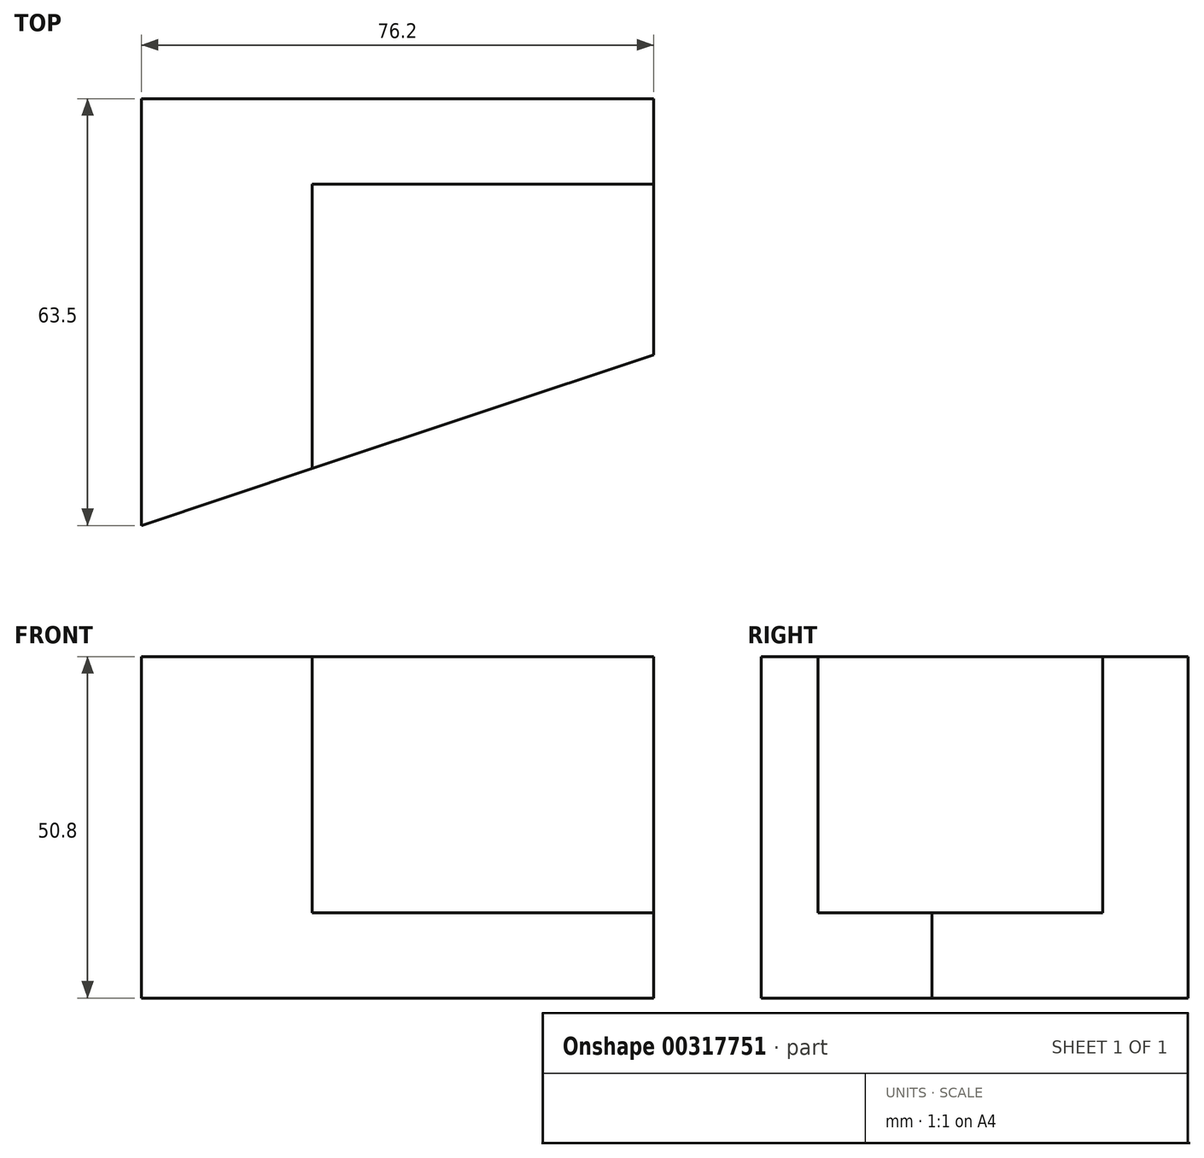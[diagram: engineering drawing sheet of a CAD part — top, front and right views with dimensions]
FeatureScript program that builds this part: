
annotation { "Feature Type Name" : "Feature", "Feature Type Description" : "" }
export const myFeature = defineFeature(function(context is Context, id is Id, definition is map)
    precondition{}
    {
        {
            var Q0;
            Q0=qCreatedBy(makeId("Top.planeOp"),FACE);
            var sketch = newSketch(context, id + "F0", { "sketchPlane" : qUnion([Q0])});
            skLineSegment(sketch, "E0.bottom", {"start": v(0, 0) * mm, "end": v(76.2, 0) * mm});
            skLineSegment(sketch, "E0.top", {"start": v(0, 63.5) * mm, "end": v(76.2, 63.5) * mm});
            skLineSegment(sketch, "E0.left", {"start": v(0, 0) * mm, "end": v(0, 63.5) * mm});
            skLineSegment(sketch, "E0.right", {"start": v(76.2, 0) * mm, "end": v(76.2, 63.5) * mm});
            skSolve(sketch);
        }
        {
            var Q0;
            Q0 = qSketchRegion(id + "F0", true);
            extrude(context, id + "F1", {"entities" : qUnion([Q0]), "depth" : 12.7 * mm});
        }
        {
            var Q0;
            Q0=makeQuery(id+"F1.opExtrude","CAP_FACE",FACE,{"disambiguationData":[OSD([sQuery(id+"F0.wireOp",EDGE,"E0.bottom"),sQuery(id+"F0.wireOp",EDGE,"E0.top"),sQuery(id+"F0.wireOp",EDGE,"E0.left"),sQuery(id+"F0.wireOp",EDGE,"E0.right")])],"isStart":false});
            var sketch = newSketch(context, id + "F2", { "sketchPlane" : qUnion([Q0])});
            skLineSegment(sketch, "E1.bottom", {"start": v(0, 0) * mm, "end": v(25.4, 0) * mm});
            skLineSegment(sketch, "E1.top", {"start": v(0, 63.5) * mm, "end": v(25.4, 63.5) * mm});
            skLineSegment(sketch, "E1.left", {"start": v(0, 0) * mm, "end": v(0, 63.5) * mm});
            skLineSegment(sketch, "E1.right", {"start": v(25.4, 0) * mm, "end": v(25.4, 50.8) * mm});
            skLineSegment(sketch, "E2.bottom", {"start": v(76.2, 63.5) * mm, "end": v(0, 63.5) * mm});
            skLineSegment(sketch, "E2.top", {"start": v(76.2, 50.8) * mm, "end": v(25.4, 50.8) * mm});
            skLineSegment(sketch, "E2.left", {"start": v(76.2, 63.5) * mm, "end": v(76.2, 50.8) * mm});
            skLineSegment(sketch, "E2.right", {"start": v(0, 63.5) * mm, "end": v(0, 50.8) * mm});
            skSolve(sketch);
        }
        {
            var Q0;
            Q0 = qSketchRegion(id + "F2", true);
            extrude(context, id + "F3", {"entities" : qUnion([Q0]), "operationType" : NewBodyOperationType.ADD, "depth" : 38.1 * mm});
        }
        {
            var Q0;
            Q0=makeQuery(id+"F3.opExtrude","CAP_FACE",FACE,{"disambiguationData":[OSD([sQuery(id+"F2.wireOp",EDGE,"E1.bottom"),sQuery(id+"F2.wireOp",EDGE,"E1.left"),sQuery(id+"F2.wireOp",EDGE,"E1.right"),sQuery(id+"F2.wireOp",EDGE,"E2.bottom"),sQuery(id+"F2.wireOp",EDGE,"E2.top"),sQuery(id+"F2.wireOp",EDGE,"E2.left"),sQuery(id+"F2.wireOp",EDGE,"E2.right")])],"isStart":false});
            var sketch = newSketch(context, id + "F4", { "sketchPlane" : qUnion([Q0])});
            skLineSegment(sketch, "E3", {"start": v(0, 0) * mm, "end": v(76.2, 0) * mm});
            skLineSegment(sketch, "E4", {"start": v(76.2, 0) * mm, "end": v(76.2, 25.4) * mm});
            skLineSegment(sketch, "E5", {"start": v(76.2, 25.4) * mm, "end": v(0, 0) * mm});
            skSolve(sketch);
        }
        {
            var Q0;
            Q0 = qSketchRegion(id + "F4", true);
            extrude(context, id + "F5", {"entities" : qUnion([Q0]), "operationType" : NewBodyOperationType.REMOVE, "endBound" : BoundingType.THROUGH_ALL, "oppositeDirection" : true, "depth" : 25.4 * mm});
        }
    });
